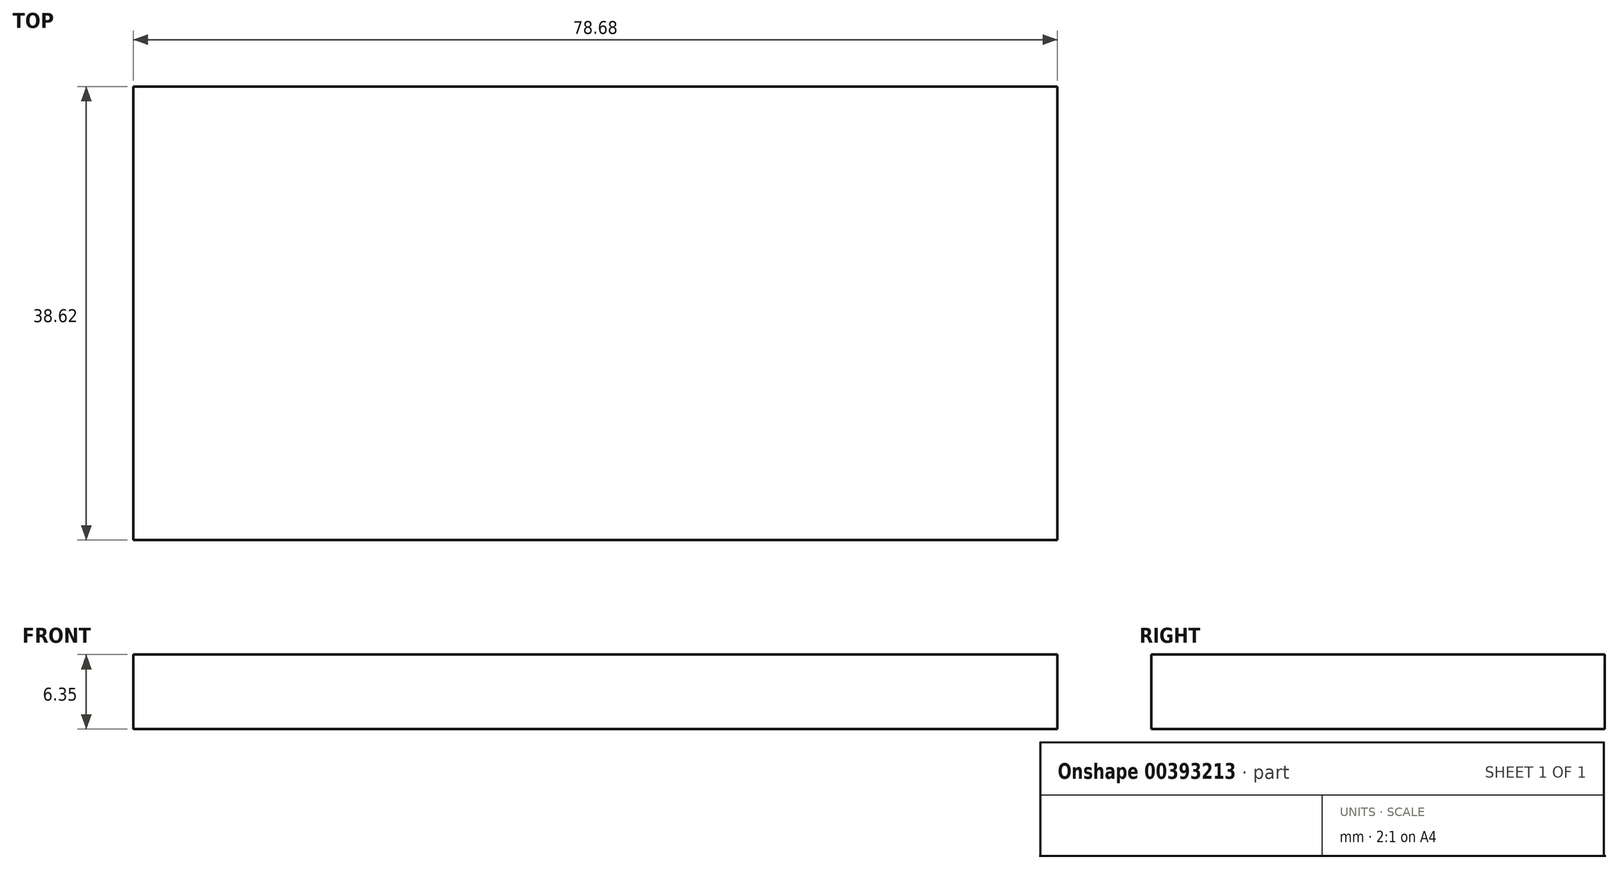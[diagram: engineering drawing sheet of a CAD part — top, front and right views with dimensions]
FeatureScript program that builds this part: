
annotation { "Feature Type Name" : "Feature", "Feature Type Description" : "" }
export const myFeature = defineFeature(function(context is Context, id is Id, definition is map)
    precondition{}
    {
        {
            var Q0;
            Q0=qCreatedBy(makeId("Top.planeOp"),FACE);
            var sketch = newSketch(context, id + "F0", { "sketchPlane" : qUnion([Q0])});
            skLineSegment(sketch, "E0.bottom", {"start": v(-39.34, -19.3) * mm, "end": v(39.34, -19.3) * mm});
            skLineSegment(sketch, "E0.top", {"start": v(-39.34, 19.3) * mm, "end": v(39.34, 19.3) * mm});
            skLineSegment(sketch, "E0.left", {"start": v(-39.34, -19.3) * mm, "end": v(-39.34, 19.3) * mm});
            skLineSegment(sketch, "E0.right", {"start": v(39.34, -19.3) * mm, "end": v(39.34, 19.3) * mm});
            skPoint(sketch, "E0.middle", {"position": v(0, 0) * mm});
            skSolve(sketch);
        }
        {
            var Q0;
            Q0=makeQuery(id+"F0.imprint","IMPRINT",FACE,{"disambiguationData":[TD([[makeQuery(id+"F0.imprint","IMPRINT",EDGE,{"derivedFrom":sQuery(id+"F0.wireOp",EDGE,"E0.bottom")}),1.0]])]});
            extrude(context, id + "F1", {"entities" : qUnion([Q0]), "depth" : 6.35 * mm});
        }
    });
